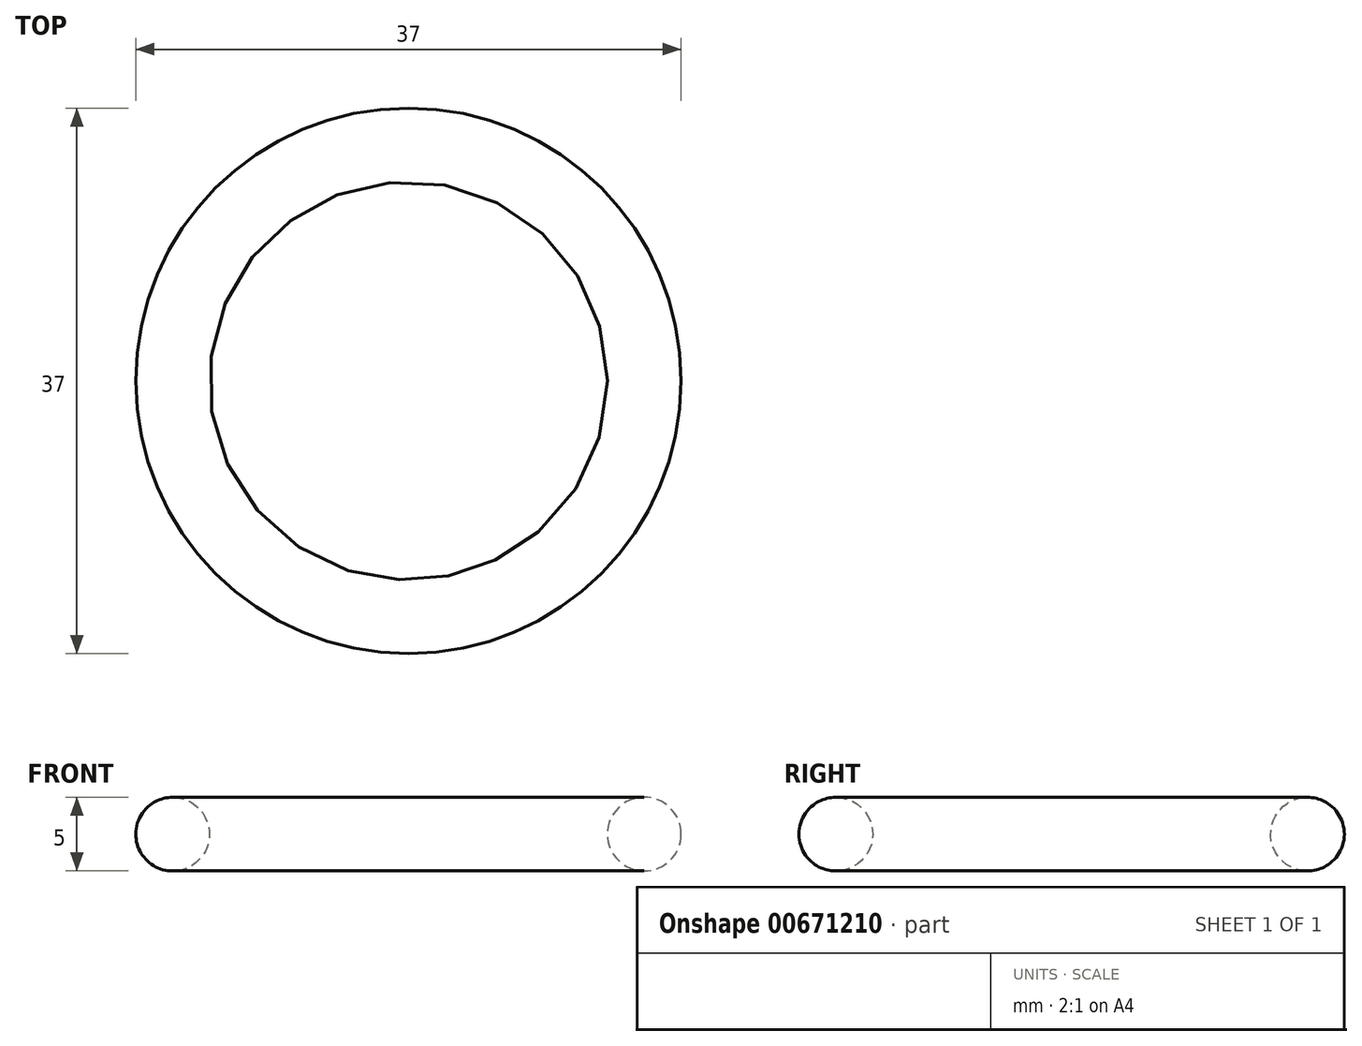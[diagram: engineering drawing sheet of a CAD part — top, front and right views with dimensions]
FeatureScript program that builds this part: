
annotation { "Feature Type Name" : "Feature", "Feature Type Description" : "" }
export const myFeature = defineFeature(function(context is Context, id is Id, definition is map)
    precondition{}
    {
        {
            var Q0;
            Q0=qCreatedBy(makeId("Front.planeOp"),FACE);
            var sketch = newSketch(context, id + "F0", { "sketchPlane" : qUnion([Q0])});
            skCircle(sketch, "E0", {"center": v(16, 0) * mm, "radius": 2.5 * mm});
            skLineSegment(sketch, "E1", {"start": v(0, 28.18) * mm, "end": v(0, -30.55) * mm, "construction": true});
            skSolve(sketch);
        }
        {
            var Q0;
            Q0=makeQuery(id+"F0.imprint","IMPRINT",FACE,{"disambiguationData":[TD([[makeQuery(id+"F0.imprint","IMPRINT",EDGE,{"derivedFrom":sQuery(id+"F0.wireOp",EDGE,"E0")}),1.0]])]});
            var Q1;
            Q1=sQuery(id+"F0.wireOp",EDGE,"E1");
            revolve(context, id + "F1", {"entities" : qUnion([Q0]), "axis" : qUnion([Q1]), "revolveType" : RevolveType.FULL});
        }
    });
